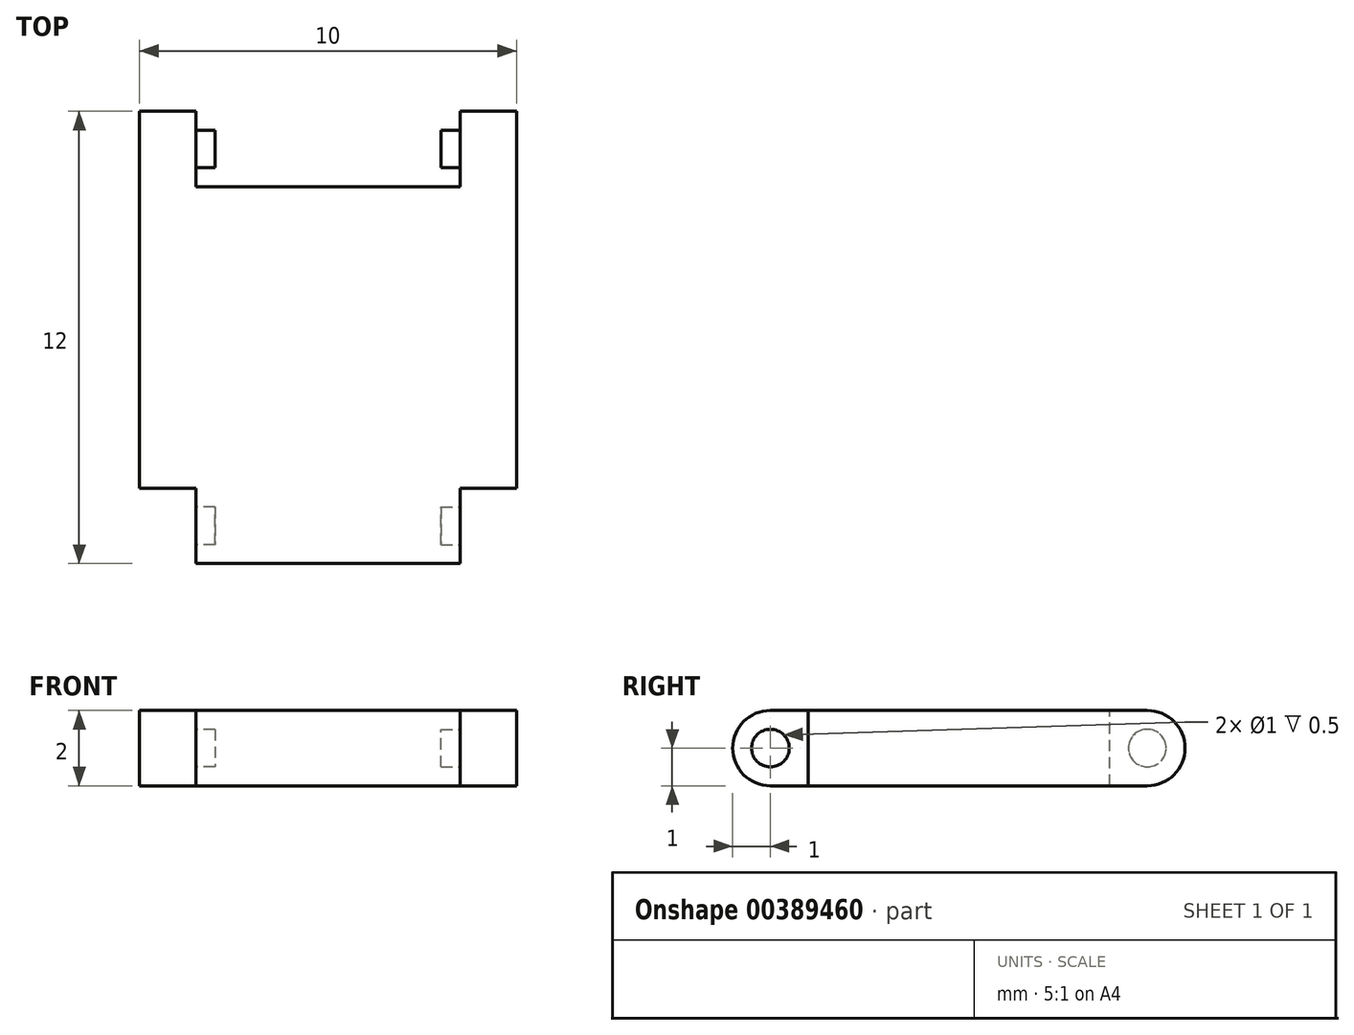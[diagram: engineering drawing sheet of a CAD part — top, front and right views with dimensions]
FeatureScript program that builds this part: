
annotation { "Feature Type Name" : "Feature", "Feature Type Description" : "" }
export const myFeature = defineFeature(function(context is Context, id is Id, definition is map)
    precondition{}
    {
        {
            var Q0;
            Q0=qCreatedBy(makeId("Right.planeOp"),FACE);
            var sketch = newSketch(context, id + "F0", { "sketchPlane" : qUnion([Q0])});
            skLineSegment(sketch, "E0.bottom", {"start": v(5, 1) * mm, "end": v(-5, 1) * mm});
            skLineSegment(sketch, "E0.top", {"start": v(5, -1) * mm, "end": v(-5, -1) * mm});
            skPoint(sketch, "E0.middle", {"position": v(0, 0) * mm});
            skArc(sketch, "E1", {"start": v(5, -1) * mm, "mid": v(6, 0) * mm, "end": v(5, 1) * mm});
            skArc(sketch, "E2", {"start": v(-5, 1) * mm, "mid": v(-6, 0) * mm, "end": v(-5, -1) * mm});
            skSolve(sketch);
        }
        {
            var Q0;
            Q0=qSketchRegion(id+"F0",true);
            extrude(context, id + "F1", {"entities" : qUnion([Q0]), "endBound" : BoundingType.SYMMETRIC, "depth" : 10 * mm});
        }
        {
            var Q0;
            Q0=makeQuery(id+"F1.opExtrude","SWEPT_FACE",FACE,{"disambiguationData":[OSD([sQuery(id+"F0.wireOp",EDGE,"E0.bottom")])]});
            var sketch = newSketch(context, id + "F2", { "sketchPlane" : qUnion([Q0])});
            skLineSegment(sketch, "E3.bottom", {"start": v(3.5, 6.1) * mm, "end": v(-3.5, 6.1) * mm});
            skLineSegment(sketch, "E3.left", {"start": v(3.5, 6.1) * mm, "end": v(3.5, 4) * mm});
            skLineSegment(sketch, "E3.right", {"start": v(-3.5, 6.1) * mm, "end": v(-3.5, 4) * mm});
            skPoint(sketch, "E3.middle", {"position": v(0, 5) * mm});
            skLineSegment(sketch, "E4", {"start": v(-3.5, 4) * mm, "end": v(3.5, 4) * mm});
            skLineSegment(sketch, "E5.bottom", {"start": v(-5, -4) * mm, "end": v(-3.5, -4) * mm});
            skLineSegment(sketch, "E5.top", {"start": v(-5, -6.5) * mm, "end": v(-3.5, -6.5) * mm});
            skLineSegment(sketch, "E5.left", {"start": v(-5, -4) * mm, "end": v(-5, -6.5) * mm});
            skLineSegment(sketch, "E5.right", {"start": v(-3.5, -4) * mm, "end": v(-3.5, -6.5) * mm});
            skLineSegment(sketch, "E6.bottom", {"start": v(5, -4) * mm, "end": v(3.5, -4) * mm});
            skLineSegment(sketch, "E6.top", {"start": v(5, -7.1) * mm, "end": v(3.5, -7.1) * mm});
            skLineSegment(sketch, "E6.left", {"start": v(5, -4) * mm, "end": v(5, -7.1) * mm});
            skLineSegment(sketch, "E6.right", {"start": v(3.5, -4) * mm, "end": v(3.5, -7.1) * mm});
            skSolve(sketch);
        }
        {
            var Q0;
            Q0=qSketchRegion(id+"F2",true);
            extrude(context, id + "F3", {"entities" : qUnion([Q0]), "operationType" : NewBodyOperationType.REMOVE, "oppositeDirection" : true, "depth" : 5 * mm});
        }
        {
            var Q0;
            Q0=makeQuery(id+"F3.boolean.opBoolean","COPY",FACE,{"derivedFrom":makeQuery(id+"F3.opExtrude","SWEPT_FACE",FACE,{"disambiguationData":[OSD([sQuery(id+"F2.wireOp",EDGE,"E5.right")])]})});
            var sketch = newSketch(context, id + "F4", { "sketchPlane" : qUnion([Q0])});
            skCircle(sketch, "E7", {"center": v(5, 0) * mm, "radius": 0.5 * mm});
            skSolve(sketch);
        }
        {
            var Q0;
            Q0=qSketchRegion(id+"F4",true);
            extrude(context, id + "F5", {"entities" : qUnion([Q0]), "operationType" : NewBodyOperationType.REMOVE, "oppositeDirection" : true, "depth" : 0.5 * mm});
        }
        {
            var Q0;
            Q0=makeQuery(id+"F3.boolean.opBoolean","COPY",FACE,{"derivedFrom":makeQuery(id+"F3.opExtrude","SWEPT_FACE",FACE,{"disambiguationData":[OSD([sQuery(id+"F2.wireOp",EDGE,"E6.right")])]})});
            var sketch = newSketch(context, id + "F6", { "sketchPlane" : qUnion([Q0])});
            skCircle(sketch, "E8", {"center": v(-5, 0) * mm, "radius": 0.5 * mm});
            skSolve(sketch);
        }
        {
            var Q0;
            Q0=qSketchRegion(id+"F6",true);
            extrude(context, id + "F7", {"entities" : qUnion([Q0]), "operationType" : NewBodyOperationType.REMOVE, "oppositeDirection" : true, "depth" : 0.5 * mm});
        }
        {
            var Q0;
            Q0=makeQuery(id+"F3.boolean.opBoolean","COPY",FACE,{"derivedFrom":makeQuery(id+"F3.opExtrude","SWEPT_FACE",FACE,{"disambiguationData":[OSD([sQuery(id+"F2.wireOp",EDGE,"E3.right")])]})});
            var sketch = newSketch(context, id + "F8", { "sketchPlane" : qUnion([Q0])});
            skCircle(sketch, "E9", {"center": v(5, 0) * mm, "radius": 0.5 * mm});
            skSolve(sketch);
        }
        {
            var Q0;
            Q0=qSketchRegion(id+"F8",true);
            extrude(context, id + "F9", {"entities" : qUnion([Q0]), "operationType" : NewBodyOperationType.ADD, "depth" : 0.5 * mm});
        }
        {
            var Q0;
            Q0=makeQuery(id+"F3.boolean.opBoolean","COPY",FACE,{"derivedFrom":makeQuery(id+"F3.opExtrude","SWEPT_FACE",FACE,{"disambiguationData":[OSD([sQuery(id+"F2.wireOp",EDGE,"E3.left")])]})});
            var sketch = newSketch(context, id + "F10", { "sketchPlane" : qUnion([Q0])});
            skCircle(sketch, "E10", {"center": v(-5, 0) * mm, "radius": 0.5 * mm});
            skSolve(sketch);
        }
        {
            var Q0;
            Q0=qSketchRegion(id+"F10",true);
            extrude(context, id + "F11", {"entities" : qUnion([Q0]), "operationType" : NewBodyOperationType.ADD, "depth" : 0.5 * mm});
        }
    });
